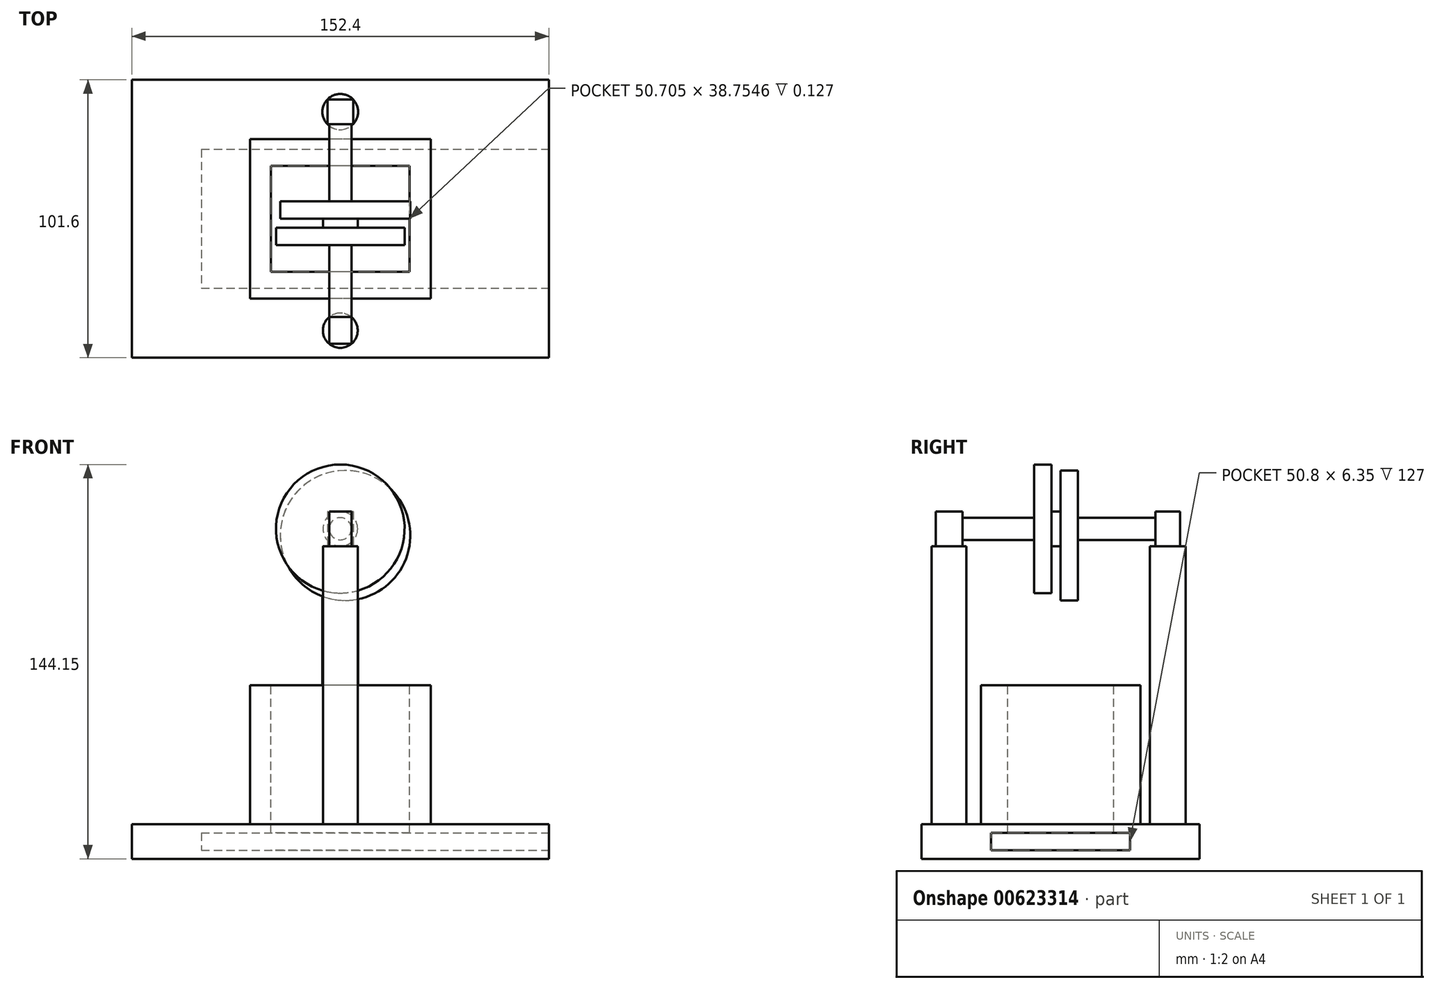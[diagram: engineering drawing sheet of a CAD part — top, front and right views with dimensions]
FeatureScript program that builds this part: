
annotation { "Feature Type Name" : "Feature", "Feature Type Description" : "" }
export const myFeature = defineFeature(function(context is Context, id is Id, definition is map)
    precondition{}
    {
        {
            var Q0;
            Q0=qCreatedBy(makeId("Front.planeOp"),FACE);
            var sketch = newSketch(context, id + "F0", { "sketchPlane" : qUnion([Q0])});
            skLineSegment(sketch, "E0", {"start": v(0, 0) * mm, "end": v(0, 12.7) * mm});
            skLineSegment(sketch, "E1", {"start": v(0, 12.7) * mm, "end": v(152.4, 12.7) * mm});
            skLineSegment(sketch, "E2", {"start": v(152.4, 12.7) * mm, "end": v(152.4, 0) * mm});
            skLineSegment(sketch, "E3", {"start": v(152.4, 0) * mm, "end": v(0, 0) * mm});
            skSolve(sketch);
        }
        {
            var Q0;
            Q0 = qSketchRegion(id + "F0", true);
            extrude(context, id + "F1", {"entities" : qUnion([Q0]), "oppositeDirection" : true, "depth" : 101.6 * mm, "offsetDistance" : 25.4 * mm});
        }
        {
            var Q0;
            Q0=makeQuery(id+"F1.opExtrude","SWEPT_FACE",FACE,{"disambiguationData":[OSD([sQuery(id+"F0.wireOp",EDGE,"E2")])]});
            var sketch = newSketch(context, id + "F2", { "sketchPlane" : qUnion([Q0])});
            skPoint(sketch, "E4.startSnap0", {"position": v(101.6, 6.35) * mm});
            skPoint(sketch, "E4.startSnap1", {"position": v(50.8, 0) * mm});
            skLineSegment(sketch, "E5", {"start": v(76.2, 6.35) * mm, "end": v(76.2, 3.17) * mm});
            skLineSegment(sketch, "E6", {"start": v(76.2, 3.17) * mm, "end": v(25.4, 3.17) * mm});
            skLineSegment(sketch, "E7", {"start": v(25.4, 3.17) * mm, "end": v(25.4, 6.35) * mm});
            skLineSegment(sketch, "E8", {"start": v(76.2, 6.35) * mm, "end": v(76.2, 9.52) * mm});
            skLineSegment(sketch, "E9", {"start": v(76.2, 9.52) * mm, "end": v(25.4, 9.52) * mm});
            skLineSegment(sketch, "E10", {"start": v(25.4, 9.52) * mm, "end": v(25.4, 6.35) * mm});
            skSolve(sketch);
        }
        {
            var Q0;
            Q0=makeQuery(id+"F2.imprint","IMPRINT",FACE,{"disambiguationData":[TD([[makeQuery(id+"F2.imprint","IMPRINT",EDGE,{"derivedFrom":sQuery(id+"F2.wireOp",EDGE,"E5")}),-1.0]])]});
            extrude(context, id + "F3", {"entities" : qUnion([Q0]), "operationType" : NewBodyOperationType.REMOVE, "oppositeDirection" : true, "depth" : 127 * mm, "offsetDistance" : 25.4 * mm});
        }
        {
            var Q0;
            Q0=makeQuery(id+"F1.opExtrude","SWEPT_FACE",FACE,{"disambiguationData":[OSD([sQuery(id+"F0.wireOp",EDGE,"E1")])]});
            var sketch = newSketch(context, id + "F4", { "sketchPlane" : qUnion([Q0])});
            skLineSegment(sketch, "E11.bottom", {"start": v(109.21, 21.7) * mm, "end": v(43.19, 21.7) * mm});
            skLineSegment(sketch, "E11.top", {"start": v(109.21, 79.9) * mm, "end": v(43.19, 79.9) * mm});
            skLineSegment(sketch, "E11.left", {"start": v(109.21, 21.7) * mm, "end": v(109.21, 79.9) * mm});
            skLineSegment(sketch, "E11.right", {"start": v(43.19, 21.7) * mm, "end": v(43.19, 79.9) * mm});
            skPoint(sketch, "E11.middle", {"position": v(76.2, 50.8) * mm});
            skPoint(sketch, "E11.middle.positionSnap0", {"position": v(152.4, 50.8) * mm});
            skPoint(sketch, "E11.middle.positionSnap1", {"position": v(76.2, 0) * mm});
            skPoint(sketch, "E11.centerSnap0", {"position": v(152.4, 50.8) * mm});
            skPoint(sketch, "E11.centerSnap1", {"position": v(76.2, 0) * mm});
            skSolve(sketch);
        }
        {
            var Q0;
            Q0=makeQuery(id+"F4.imprint","IMPRINT",FACE,{"disambiguationData":[TD([[makeQuery(id+"F4.imprint","IMPRINT",EDGE,{"derivedFrom":sQuery(id+"F4.wireOp",EDGE,"E11.bottom")}),-1.0]])]});
            extrude(context, id + "F5", {"entities" : qUnion([Q0]), "operationType" : NewBodyOperationType.ADD, "depth" : 50.8 * mm, "offsetDistance" : 25.4 * mm});
        }
        {
            var Q0;
            Q0=makeQuery(id+"F5.opExtrude","CAP_FACE",FACE,{"disambiguationData":[OSD([sQuery(id+"F4.wireOp",EDGE,"E11.bottom"),sQuery(id+"F4.wireOp",EDGE,"E11.top"),sQuery(id+"F4.wireOp",EDGE,"E11.left"),sQuery(id+"F4.wireOp",EDGE,"E11.right")])],"isStart":false});
            var sketch = newSketch(context, id + "F6", { "sketchPlane" : qUnion([Q0])});
            skLineSegment(sketch, "E12.bottom", {"start": v(101.55, 31.42) * mm, "end": v(50.85, 31.42) * mm});
            skLineSegment(sketch, "E12.top", {"start": v(101.55, 70.18) * mm, "end": v(50.85, 70.18) * mm});
            skLineSegment(sketch, "E12.left", {"start": v(101.55, 31.42) * mm, "end": v(101.55, 70.18) * mm});
            skLineSegment(sketch, "E12.right", {"start": v(50.85, 31.42) * mm, "end": v(50.85, 70.18) * mm});
            skPoint(sketch, "E12.middle", {"position": v(76.2, 50.8) * mm});
            skPoint(sketch, "E12.middle.positionSnap0", {"position": v(109.21, 50.8) * mm});
            skPoint(sketch, "E12.middle.positionSnap1", {"position": v(76.2, 21.7) * mm});
            skPoint(sketch, "E12.centerSnap0", {"position": v(109.21, 50.8) * mm});
            skPoint(sketch, "E12.centerSnap1", {"position": v(76.2, 21.7) * mm});
            skSolve(sketch);
        }
        {
            var Q0;
            Q0=makeQuery(id+"F6.imprint","IMPRINT",FACE,{"disambiguationData":[TD([[makeQuery(id+"F6.imprint","IMPRINT",EDGE,{"derivedFrom":sQuery(id+"F6.wireOp",EDGE,"E12.bottom")}),-1.0]])]});
            extrude(context, id + "F7", {"entities" : qUnion([Q0]), "operationType" : NewBodyOperationType.REMOVE, "oppositeDirection" : true, "depth" : 60.45 * mm, "offsetDistance" : 25.4 * mm});
        }
        {
            var Q0;
            Q0=makeQuery(id+"F1.opExtrude","SWEPT_FACE",FACE,{"disambiguationData":[OSD([sQuery(id+"F0.wireOp",EDGE,"E1")])]});
            var sketch = newSketch(context, id + "F8", { "sketchPlane" : qUnion([Q0])});
            skCircle(sketch, "E13", {"center": v(76.2, 9.99) * mm, "radius": 6.36 * mm});
            skPoint(sketch, "E13.centerSnap0", {"position": v(76.2, 0) * mm});
            skSolve(sketch);
        }
        {
            var Q0;
            Q0=makeQuery(id+"F8.imprint","IMPRINT",FACE,{"disambiguationData":[TD([[makeQuery(id+"F8.imprint","IMPRINT",EDGE,{"derivedFrom":sQuery(id+"F8.wireOp",EDGE,"E13")}),1.0]])]});
            extrude(context, id + "F9", {"entities" : qUnion([Q0]), "depth" : 101.6 * mm, "offsetDistance" : 25.4 * mm});
        }
        {
            var Q0;
            Q0=makeQuery(id+"F1.opExtrude","SWEPT_FACE",FACE,{"disambiguationData":[OSD([sQuery(id+"F0.wireOp",EDGE,"E1")])]});
            var sketch = newSketch(context, id + "F10", { "sketchPlane" : qUnion([Q0])});
            skCircle(sketch, "E14", {"center": v(76.2, 89.93) * mm, "radius": 6.53 * mm});
            skPoint(sketch, "E14.centerSnap0", {"position": v(76.2, 101.6) * mm});
            skSolve(sketch);
        }
        {
            var Q0;
            Q0=makeQuery(id+"F10.imprint","IMPRINT",FACE,{"disambiguationData":[TD([[makeQuery(id+"F10.imprint","IMPRINT",EDGE,{"derivedFrom":sQuery(id+"F10.wireOp",EDGE,"E14")}),1.0]])]});
            extrude(context, id + "F11", {"entities" : qUnion([Q0]), "depth" : 101.6 * mm, "offsetDistance" : 25.4 * mm});
        }
        {
            var Q0;
            Q0=makeQuery(id+"F9.opExtrude","CAP_FACE",FACE,{"disambiguationData":[OSD([sQuery(id+"F8.wireOp",EDGE,"E13")])],"isStart":false});
            var sketch = newSketch(context, id + "F12", { "sketchPlane" : qUnion([Q0])});
            skLineSegment(sketch, "E15.bottom", {"start": v(80.27, 5.1) * mm, "end": v(72.13, 5.1) * mm});
            skLineSegment(sketch, "E15.top", {"start": v(80.27, 14.88) * mm, "end": v(72.13, 14.88) * mm});
            skLineSegment(sketch, "E15.left", {"start": v(80.27, 5.1) * mm, "end": v(80.27, 14.88) * mm});
            skLineSegment(sketch, "E15.right", {"start": v(72.13, 5.1) * mm, "end": v(72.13, 14.88) * mm});
            skPoint(sketch, "E15.middle", {"position": v(76.2, 9.99) * mm});
            skSolve(sketch);
        }
        {
            var Q0;
            Q0=makeQuery(id+"F11.opExtrude","CAP_FACE",FACE,{"disambiguationData":[OSD([sQuery(id+"F10.wireOp",EDGE,"E14")])],"isStart":false});
            var sketch = newSketch(context, id + "F13", { "sketchPlane" : qUnion([Q0])});
            skLineSegment(sketch, "E16.bottom", {"start": v(80.9, 85.39) * mm, "end": v(71.5, 85.39) * mm});
            skLineSegment(sketch, "E16.top", {"start": v(80.9, 94.46) * mm, "end": v(71.5, 94.46) * mm});
            skLineSegment(sketch, "E16.left", {"start": v(80.9, 85.39) * mm, "end": v(80.9, 94.46) * mm});
            skLineSegment(sketch, "E16.right", {"start": v(71.5, 85.39) * mm, "end": v(71.5, 94.46) * mm});
            skPoint(sketch, "E16.middle", {"position": v(76.2, 89.93) * mm});
            skSolve(sketch);
        }
        {
            var Q0;
            Q0=makeQuery(id+"F12.imprint","IMPRINT",FACE,{"disambiguationData":[TD([[makeQuery(id+"F12.imprint","IMPRINT",EDGE,{"derivedFrom":sQuery(id+"F12.wireOp",EDGE,"E15.bottom")}),-1.0]])]});
            extrude(context, id + "F14", {"entities" : qUnion([Q0]), "operationType" : NewBodyOperationType.ADD, "depth" : 12.7 * mm, "offsetDistance" : 25.4 * mm});
        }
        {
            var Q0;
            Q0=makeQuery(id+"F13.imprint","IMPRINT",FACE,{"disambiguationData":[TD([[makeQuery(id+"F13.imprint","IMPRINT",EDGE,{"derivedFrom":sQuery(id+"F13.wireOp",EDGE,"E16.bottom")}),-1.0]])]});
            extrude(context, id + "F15", {"entities" : qUnion([Q0]), "operationType" : NewBodyOperationType.ADD, "depth" : 12.7 * mm, "offsetDistance" : 25.4 * mm});
        }
        {
            var Q0;
            Q0=makeQuery(id+"F15.opExtrude","SWEPT_FACE",FACE,{"disambiguationData":[OSD([sQuery(id+"F13.wireOp",EDGE,"E16.bottom")])]});
            var sketch = newSketch(context, id + "F16", { "sketchPlane" : qUnion([Q0])});
            skCircle(sketch, "E17", {"center": v(76.2, 120.65) * mm, "radius": 4.05 * mm});
            skPoint(sketch, "E17.centerSnap0", {"position": v(80.9, 120.65) * mm});
            skPoint(sketch, "E17.centerSnap1", {"position": v(76.2, 127) * mm});
            skSolve(sketch);
        }
        {
            var Q0;
            Q0=makeQuery(id+"F16.imprint","IMPRINT",FACE,{"disambiguationData":[TD([[makeQuery(id+"F16.imprint","IMPRINT",EDGE,{"derivedFrom":sQuery(id+"F16.wireOp",EDGE,"E17")}),1.0]])]});
            extrude(context, id + "F17", {"entities" : qUnion([Q0]), "operationType" : NewBodyOperationType.ADD, "depth" : 76.2 * mm, "offsetDistance" : 25.4 * mm});
        }
        {
            var Q0;
            Q0=qCreatedBy(makeId("Front.planeOp"),FACE);
            cPlane(context, id + "F18", {"entities" : qUnion([Q0]), "cplaneType" : CPlaneType.OFFSET, "offset" : 50.8 * mm, "oppositeDirection" : true, "width" : 152.4 * mm, "height" : 152.4 * mm});
        }
        {
            var Q0;
            Q0=qCreatedBy(id+"F18.planeOp",FACE);
            var sketch = newSketch(context, id + "F19", { "sketchPlane" : qUnion([Q0])});
            skCircle(sketch, "E18", {"center": v(78, 118.2) * mm, "radius": 23.76 * mm});
            skSolve(sketch);
        }
        {
            var Q0;
            Q0 = qSketchRegion(id + "F19", true);
            extrude(context, id + "F20", {"entities" : qUnion([Q0]), "operationType" : NewBodyOperationType.ADD, "oppositeDirection" : true, "depth" : 6.35 * mm, "offsetDistance" : 25.4 * mm});
        }
        {
            var Q0;
            Q0=makeQuery(id+"F20.opExtrude","CAP_FACE",FACE,{"disambiguationData":[OSD([sQuery(id+"F19.wireOp",EDGE,"E18")])],"isStart":true});
            var sketch = newSketch(context, id + "F21", { "sketchPlane" : qUnion([Q0])});
            skCircle(sketch, "E19", {"center": v(76.2, 120.65) * mm, "radius": 6.35 * mm});
            skSolve(sketch);
        }
        {
            var Q0;
            Q0 = qSketchRegion(id + "F21", true);
            extrude(context, id + "F22", {"entities" : qUnion([Q0]), "operationType" : NewBodyOperationType.ADD, "depth" : 3.3 * mm, "offsetDistance" : 25.4 * mm});
        }
        {
            var Q0;
            Q0=makeQuery(id+"F22.opExtrude","CAP_FACE",FACE,{"disambiguationData":[OSD([sQuery(id+"F21.wireOp",EDGE,"E19")])],"isStart":false});
            var sketch = newSketch(context, id + "F23", { "sketchPlane" : qUnion([Q0])});
            skCircle(sketch, "E20", {"center": v(76.2, 120.65) * mm, "radius": 23.5 * mm});
            skSolve(sketch);
        }
        {
            var Q0;
            Q0 = qSketchRegion(id + "F23", true);
            extrude(context, id + "F24", {"entities" : qUnion([Q0]), "operationType" : NewBodyOperationType.ADD, "depth" : 6.35 * mm, "offsetDistance" : 25.4 * mm});
        }
    });
